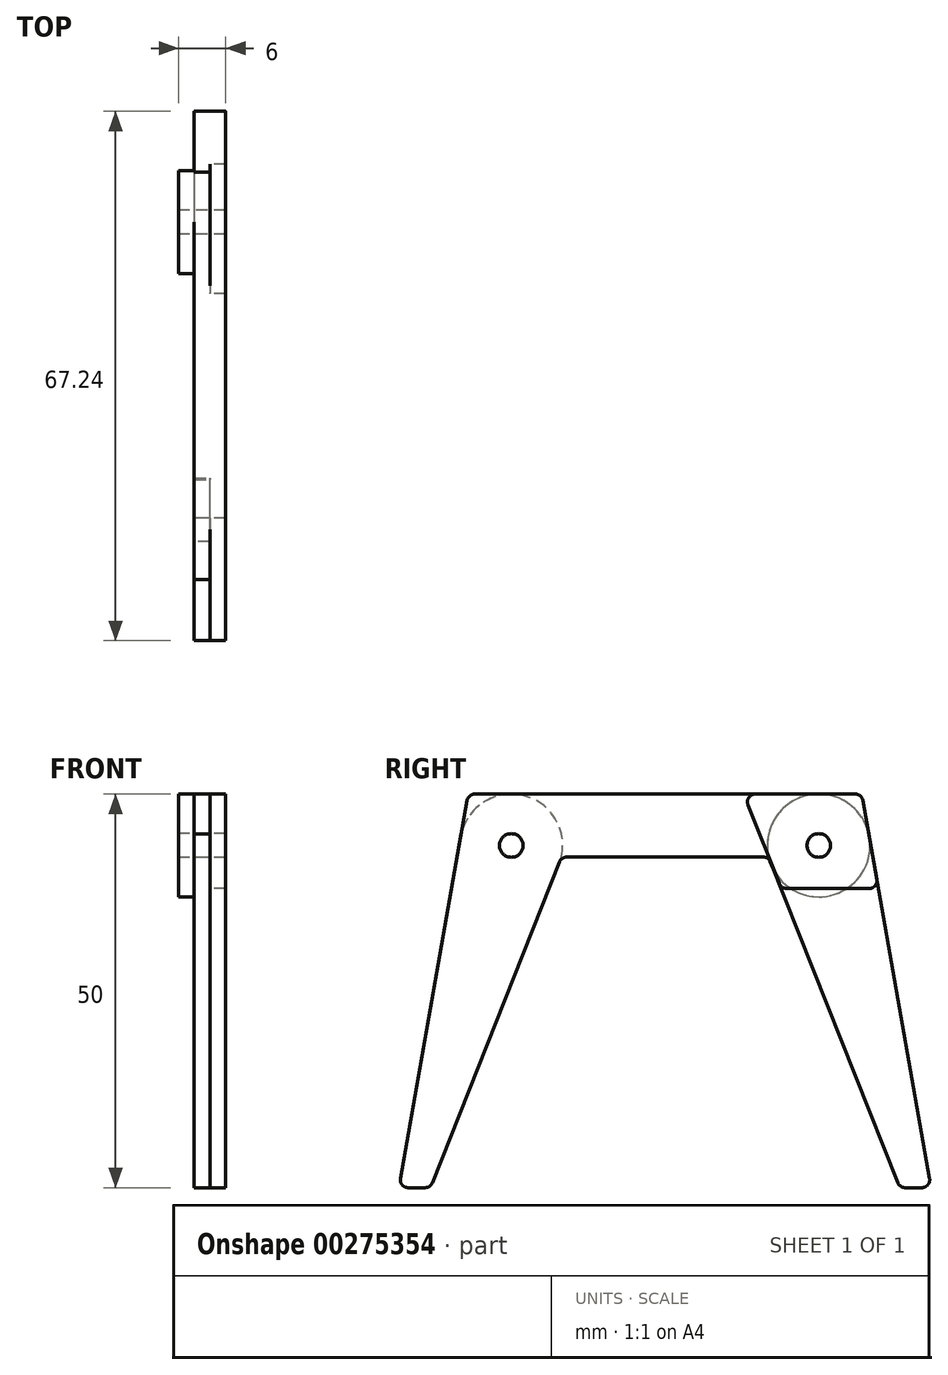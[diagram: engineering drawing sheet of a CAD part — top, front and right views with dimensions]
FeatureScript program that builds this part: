
annotation { "Feature Type Name" : "Feature", "Feature Type Description" : "" }
export const myFeature = defineFeature(function(context is Context, id is Id, definition is map)
    precondition{}
    {
        {
            var Q0;
            Q0=qCreatedBy(makeId("Right.planeOp"),FACE);
            var sketch = newSketch(context, id + "F0", { "sketchPlane" : qUnion([Q0])});
            skLineSegment(sketch, "E0", {"start": v(25.15, 3.17) * mm, "end": v(33.6, -44.83) * mm});
            skLineSegment(sketch, "E1", {"start": v(32.62, -46) * mm, "end": v(30.5, -46) * mm});
            skLineSegment(sketch, "E2", {"start": v(29.57, -45.37) * mm, "end": v(13.42, -4.63) * mm});
            skLineSegment(sketch, "E3", {"start": v(12.5, -4) * mm, "end": v(0, -4) * mm});
            skLineSegment(sketch, "E4", {"start": v(0, -4) * mm, "end": v(0, 4) * mm});
            skLineSegment(sketch, "E5", {"start": v(13.17, -4) * mm, "end": v(10, 4) * mm, "construction": true});
            skLineSegment(sketch, "E6", {"start": v(0, 4) * mm, "end": v(10, 4) * mm});
            skLineSegment(sketch, "E7", {"start": v(24.16, 4) * mm, "end": v(10, 4) * mm});
            skPoint(sketch, "E8.visualSharp", {"position": v(25, 4) * mm});
            skArc(sketch, "E8.filletArc", {"start": v(25.15, 3.17) * mm, "mid": v(24.8, 3.77) * mm, "end": v(24.16, 4) * mm});
            skPoint(sketch, "E9.visualSharp", {"position": v(13.17, -4) * mm});
            skArc(sketch, "E9.filletArc", {"start": v(13.42, -4.63) * mm, "mid": v(13.05, -4.17) * mm, "end": v(12.5, -4) * mm});
            skPoint(sketch, "E10.visualSharp", {"position": v(29.82, -46) * mm});
            skArc(sketch, "E10.filletArc", {"start": v(29.57, -45.37) * mm, "mid": v(29.93, -45.83) * mm, "end": v(30.5, -46) * mm});
            skPoint(sketch, "E11.visualSharp", {"position": v(33.82, -46) * mm});
            skArc(sketch, "E11.filletArc", {"start": v(32.62, -46) * mm, "mid": v(33.4, -45.64) * mm, "end": v(33.6, -44.83) * mm});
            skSolve(sketch);
        }
        {
            var Q0;
            Q0=qCreatedBy(makeId("Right.planeOp"),FACE);
            var sketch = newSketch(context, id + "F1", { "sketchPlane" : qUnion([Q0])});
            skLineSegment(sketch, "E12", {"start": v(25.9, -1.06) * mm, "end": v(33.6, -44.83) * mm});
            skLineSegment(sketch, "E13", {"start": v(32.62, -46) * mm, "end": v(30.5, -46) * mm});
            skLineSegment(sketch, "E14", {"start": v(29.57, -45.37) * mm, "end": v(13.42, -4.63) * mm});
            skLineSegment(sketch, "E15", {"start": v(12.5, -4) * mm, "end": v(0, -4) * mm});
            skLineSegment(sketch, "E16", {"start": v(0, -4) * mm, "end": v(0, 4) * mm});
            skLineSegment(sketch, "E17", {"start": v(13.17, -4) * mm, "end": v(10, 4) * mm, "construction": true});
            skLineSegment(sketch, "E18", {"start": v(0, 4) * mm, "end": v(10, 4) * mm});
            skLineSegment(sketch, "E19", {"start": v(25, 4) * mm, "end": v(19.53, 4) * mm, "construction": true});
            skArc(sketch, "E20", {"start": v(25.9, -1.06) * mm, "mid": v(23.6, 2.58) * mm, "end": v(19.53, 4) * mm});
            skLineSegment(sketch, "E21", {"start": v(13.17, -4) * mm, "end": v(25.9, -1.06) * mm, "construction": true});
            skLineSegment(sketch, "E22", {"start": v(25.9, -1.06) * mm, "end": v(25, 4) * mm, "construction": true});
            skLineSegment(sketch, "E23", {"start": v(19.53, 4) * mm, "end": v(10, 4) * mm});
            skPoint(sketch, "E24.visualSharp", {"position": v(13.17, -4) * mm});
            skArc(sketch, "E24.filletArc", {"start": v(13.42, -4.63) * mm, "mid": v(13.05, -4.17) * mm, "end": v(12.5, -4) * mm});
            skPoint(sketch, "E25.visualSharp", {"position": v(29.82, -46) * mm});
            skArc(sketch, "E25.filletArc", {"start": v(29.57, -45.37) * mm, "mid": v(29.93, -45.83) * mm, "end": v(30.5, -46) * mm});
            skPoint(sketch, "E26.visualSharp", {"position": v(33.82, -46) * mm});
            skArc(sketch, "E26.filletArc", {"start": v(32.62, -46) * mm, "mid": v(33.4, -45.64) * mm, "end": v(33.6, -44.83) * mm});
            skSolve(sketch);
        }
        {
            var Q0;
            Q0=qCreatedBy(makeId("Right.planeOp"),FACE);
            var sketch = newSketch(context, id + "F2", { "sketchPlane" : qUnion([Q0])});
            skLineSegment(sketch, "E27", {"start": v(25.9, -1.06) * mm, "end": v(33.6, -44.83) * mm});
            skLineSegment(sketch, "E28", {"start": v(32.62, -46) * mm, "end": v(30.5, -46) * mm});
            skLineSegment(sketch, "E29", {"start": v(29.57, -45.37) * mm, "end": v(13.17, -4) * mm});
            skLineSegment(sketch, "E30", {"start": v(13.17, -4) * mm, "end": v(0, -4) * mm, "construction": true});
            skLineSegment(sketch, "E31", {"start": v(0, -4) * mm, "end": v(0, 4) * mm, "construction": true});
            skLineSegment(sketch, "E32", {"start": v(13.17, -4) * mm, "end": v(10, 4) * mm, "construction": true});
            skLineSegment(sketch, "E33", {"start": v(0, 4) * mm, "end": v(10, 4) * mm, "construction": true});
            skLineSegment(sketch, "E34", {"start": v(25, 4) * mm, "end": v(19.53, 4) * mm, "construction": true});
            skLineSegment(sketch, "E35", {"start": v(13.17, -4) * mm, "end": v(25.9, -1.06) * mm, "construction": true});
            skLineSegment(sketch, "E36", {"start": v(25.9, -1.06) * mm, "end": v(25, 4) * mm, "construction": true});
            skLineSegment(sketch, "E37", {"start": v(19.53, 4) * mm, "end": v(10, 4) * mm, "construction": true});
            skArc(sketch, "E38", {"start": v(25.9, -1.06) * mm, "mid": v(18.06, 3.83) * mm, "end": v(13.17, -4) * mm});
            skPoint(sketch, "E39.visualSharp", {"position": v(29.82, -46) * mm});
            skArc(sketch, "E39.filletArc", {"start": v(29.57, -45.37) * mm, "mid": v(29.93, -45.83) * mm, "end": v(30.5, -46) * mm});
            skPoint(sketch, "E40.visualSharp", {"position": v(33.82, -46) * mm});
            skArc(sketch, "E40.filletArc", {"start": v(32.62, -46) * mm, "mid": v(33.4, -45.64) * mm, "end": v(33.6, -44.83) * mm});
            skSolve(sketch);
        }
        {
            var Q0;
            Q0=qCreatedBy(makeId("Right.planeOp"),FACE);
            var sketch = newSketch(context, id + "F3", { "sketchPlane" : qUnion([Q0])});
            skLineSegment(sketch, "E41", {"start": v(25.9, -1.06) * mm, "end": v(33.6, -44.83) * mm, "construction": true});
            skLineSegment(sketch, "E42", {"start": v(32.62, -46) * mm, "end": v(30.5, -46) * mm, "construction": true});
            skLineSegment(sketch, "E43", {"start": v(29.57, -45.37) * mm, "end": v(13.17, -4) * mm, "construction": true});
            skLineSegment(sketch, "E44", {"start": v(13.17, -4) * mm, "end": v(0, -4) * mm, "construction": true});
            skLineSegment(sketch, "E45", {"start": v(0, -4) * mm, "end": v(0, 4) * mm, "construction": true});
            skLineSegment(sketch, "E46", {"start": v(13.17, -4) * mm, "end": v(10, 4) * mm, "construction": true});
            skLineSegment(sketch, "E47", {"start": v(0, 4) * mm, "end": v(10, 4) * mm, "construction": true});
            skLineSegment(sketch, "E48", {"start": v(25, 4) * mm, "end": v(19.53, 4) * mm, "construction": true});
            skLineSegment(sketch, "E49", {"start": v(13.17, -4) * mm, "end": v(25.9, -1.06) * mm, "construction": true});
            skLineSegment(sketch, "E50", {"start": v(25.9, -1.06) * mm, "end": v(25, 4) * mm, "construction": true});
            skLineSegment(sketch, "E51", {"start": v(19.53, 4) * mm, "end": v(10, 4) * mm, "construction": true});
            skArc(sketch, "E52", {"start": v(25.9, -1.06) * mm, "mid": v(18.06, 3.83) * mm, "end": v(13.17, -4) * mm, "construction": true});
            skPoint(sketch, "E53.visualSharp", {"position": v(29.82, -46) * mm});
            skArc(sketch, "E53.filletArc", {"start": v(29.57, -45.37) * mm, "mid": v(29.93, -45.83) * mm, "end": v(30.5, -46) * mm, "construction": true});
            skPoint(sketch, "E54.visualSharp", {"position": v(33.82, -46) * mm});
            skArc(sketch, "E54.filletArc", {"start": v(32.62, -46) * mm, "mid": v(33.4, -45.64) * mm, "end": v(33.6, -44.83) * mm, "construction": true});
            skCircle(sketch, "E55", {"center": v(19.53, -2.53) * mm, "radius": 1.5 * mm});
            skCircle(sketch, "E56.MirrorC", {"center": v(-19.53, -2.53) * mm, "radius": 1.5 * mm});
            skSolve(sketch);
        }
        {
            var Q0;
            Q0=qCreatedBy(makeId("Right.planeOp"),FACE);
            var sketch = newSketch(context, id + "F4", { "sketchPlane" : qUnion([Q0])});
            skLineSegment(sketch, "E57", {"start": v(25.9, -1.06) * mm, "end": v(26.9, -6.83) * mm});
            skLineSegment(sketch, "E58", {"start": v(32.62, -46) * mm, "end": v(30.5, -46) * mm, "construction": true});
            skLineSegment(sketch, "E59", {"start": v(29.57, -45.37) * mm, "end": v(14.76, -8) * mm, "construction": true});
            skLineSegment(sketch, "E60", {"start": v(13.17, -4) * mm, "end": v(0, -4) * mm, "construction": true});
            skLineSegment(sketch, "E61", {"start": v(0, -4) * mm, "end": v(0, 4) * mm, "construction": true});
            skLineSegment(sketch, "E62", {"start": v(13.17, -4) * mm, "end": v(10.54, 2.63) * mm});
            skLineSegment(sketch, "E63", {"start": v(0, 4) * mm, "end": v(10, 4) * mm, "construction": true});
            skLineSegment(sketch, "E64", {"start": v(24.16, 4) * mm, "end": v(19.53, 4) * mm});
            skLineSegment(sketch, "E65", {"start": v(13.17, -4) * mm, "end": v(25.9, -1.06) * mm, "construction": true});
            skLineSegment(sketch, "E66", {"start": v(25.9, -1.06) * mm, "end": v(25.15, 3.17) * mm});
            skLineSegment(sketch, "E67", {"start": v(19.53, 4) * mm, "end": v(11.47, 4) * mm});
            skArc(sketch, "E68", {"start": v(25.9, -1.06) * mm, "mid": v(18.06, 3.83) * mm, "end": v(13.17, -4) * mm, "construction": true});
            skPoint(sketch, "E69.visualSharp", {"position": v(29.82, -46) * mm});
            skArc(sketch, "E69.filletArc", {"start": v(29.57, -45.37) * mm, "mid": v(29.93, -45.83) * mm, "end": v(30.5, -46) * mm, "construction": true});
            skPoint(sketch, "E70.visualSharp", {"position": v(33.82, -46) * mm});
            skArc(sketch, "E70.filletArc", {"start": v(32.62, -46) * mm, "mid": v(33.4, -45.64) * mm, "end": v(33.6, -44.83) * mm, "construction": true});
            skCircle(sketch, "E71", {"center": v(19.53, -2.53) * mm, "radius": 1.5 * mm});
            skLineSegment(sketch, "E72", {"start": v(15.44, -8) * mm, "end": v(25.92, -8) * mm});
            skLineSegment(sketch, "E73", {"start": v(14.5, -7.37) * mm, "end": v(13.17, -4) * mm});
            skLineSegment(sketch, "E74", {"start": v(27.12, -8) * mm, "end": v(33.6, -44.83) * mm, "construction": true});
            skPoint(sketch, "E75.visualSharp", {"position": v(25, 4) * mm});
            skArc(sketch, "E75.filletArc", {"start": v(25.15, 3.17) * mm, "mid": v(24.8, 3.77) * mm, "end": v(24.16, 4) * mm});
            skPoint(sketch, "E76.visualSharp", {"position": v(27.12, -8) * mm});
            skArc(sketch, "E76.filletArc", {"start": v(25.92, -8) * mm, "mid": v(26.7, -7.64) * mm, "end": v(26.9, -6.83) * mm});
            skPoint(sketch, "E77.visualSharp", {"position": v(14.76, -8) * mm});
            skArc(sketch, "E77.filletArc", {"start": v(14.5, -7.37) * mm, "mid": v(14.87, -7.83) * mm, "end": v(15.44, -8) * mm});
            skPoint(sketch, "E78.visualSharp", {"position": v(10, 4) * mm});
            skArc(sketch, "E78.filletArc", {"start": v(11.47, 4) * mm, "mid": v(10.64, 3.56) * mm, "end": v(10.54, 2.63) * mm});
            skSolve(sketch);
        }
        {
            var Q0;
            Q0=makeQuery(id+"F0.imprint","IMPRINT",FACE,{"disambiguationData":[TD([[makeQuery(id+"F0.imprint","IMPRINT",EDGE,{"derivedFrom":sQuery(id+"F0.wireOp",EDGE,"E0")}),-1.0]])]});
            extrude(context, id + "F5", {"entities" : qUnion([Q0]), "depth" : 2 * mm, "offsetDistance" : 25 * mm});
        }
        {
            var Q0;
            Q0=makeQuery(id+"F5.opExtrude","SWEPT_BODY",BODY,{"disambiguationData":[OSD([sQuery(id+"F0.wireOp",EDGE,"E0"),sQuery(id+"F0.wireOp",EDGE,"E1"),sQuery(id+"F0.wireOp",EDGE,"E2"),sQuery(id+"F0.wireOp",EDGE,"E3"),sQuery(id+"F0.wireOp",EDGE,"E4"),sQuery(id+"F0.wireOp",EDGE,"E6"),sQuery(id+"F0.wireOp",EDGE,"E7")])]});
            var Q1;
            Q1=qCreatedBy(makeId("Front.planeOp"),FACE);
            mirror(context, id + "F6", {"operationType" : NewBodyOperationType.ADD, "entities" : qUnion([Q0]), "mirrorPlane" : qUnion([Q1])});
        }
        {
            var Q0;
            Q0=makeQuery(id+"F1.imprint","IMPRINT",FACE,{"disambiguationData":[TD([[makeQuery(id+"F1.imprint","IMPRINT",EDGE,{"derivedFrom":sQuery(id+"F1.wireOp",EDGE,"E12")}),-1.0]])]});
            extrude(context, id + "F7", {"entities" : qUnion([Q0]), "oppositeDirection" : true, "depth" : 2 * mm, "offsetDistance" : 25 * mm});
        }
        {
            var Q0;
            Q0=makeQuery(id+"F7.opExtrude","SWEPT_BODY",BODY,{"disambiguationData":[OSD([sQuery(id+"F1.wireOp",EDGE,"E12"),sQuery(id+"F1.wireOp",EDGE,"E13"),sQuery(id+"F1.wireOp",EDGE,"E14"),sQuery(id+"F1.wireOp",EDGE,"E15"),sQuery(id+"F1.wireOp",EDGE,"E16"),sQuery(id+"F1.wireOp",EDGE,"E18"),sQuery(id+"F1.wireOp",EDGE,"E20"),sQuery(id+"F1.wireOp",EDGE,"E23")])]});
            var Q1;
            Q1=qCreatedBy(makeId("Front.planeOp"),FACE);
            mirror(context, id + "F8", {"operationType" : NewBodyOperationType.ADD, "entities" : qUnion([Q0]), "mirrorPlane" : qUnion([Q1])});
        }
        {
            var Q0;
            Q0 = qSketchRegion(id + "F2", true);
            extrude(context, id + "F9", {"entities" : qUnion([Q0]), "oppositeDirection" : true, "depth" : 2 * mm, "offsetDistance" : 25 * mm});
        }
        {
            var Q0;
            Q0=makeQuery(id+"F9.opExtrude","SWEPT_BODY",BODY,{"disambiguationData":[OSD([sQuery(id+"F2.wireOp",EDGE,"E27"),sQuery(id+"F2.wireOp",EDGE,"E28"),sQuery(id+"F2.wireOp",EDGE,"E29"),sQuery(id+"F2.wireOp",EDGE,"E38")])]});
            var Q1;
            Q1=qCreatedBy(makeId("Front.planeOp"),FACE);
            mirror(context, id + "F10", {"entities" : qUnion([Q0]), "mirrorPlane" : qUnion([Q1])});
        }
        {
            var Q0;
            Q0 = qSketchRegion(id + "F3", true);
            var Q1;
            Q1=sQuery(id+"F3.wireOp",EDGE,"E55");
            extrude(context, id + "F11", {"entities" : qUnion([Q0]), "operationType" : NewBodyOperationType.REMOVE, "surfaceEntities" : qUnion([Q1]), "depth" : 25 * mm, "offsetDistance" : 25 * mm, "symmetric" : true});
        }
        {
            var Q0;
            Q0=makeQuery(id+"F9.opExtrude","CAP_FACE",FACE,{"disambiguationData":[OSD([sQuery(id+"F2.wireOp",EDGE,"E27"),sQuery(id+"F2.wireOp",EDGE,"E28"),sQuery(id+"F2.wireOp",EDGE,"E29"),sQuery(id+"F2.wireOp",EDGE,"E38"),sQuery(id+"F2.wireOp",EDGE,"E39.filletArc"),sQuery(id+"F2.wireOp",EDGE,"E40.filletArc")])],"isStart":false});
            var sketch = newSketch(context, id + "F12", { "sketchPlane" : qUnion([Q0])});
            skCircle(sketch, "E79", {"center": v(-19.53, -2.53) * mm, "radius": 1.5 * mm});
            skCircle(sketch, "E80", {"center": v(-19.53, -2.53) * mm, "radius": 6.53 * mm});
            skSolve(sketch);
        }
        {
            var Q0;
            Q0 = qSketchRegion(id + "F12", true);
            extrude(context, id + "F13", {"entities" : qUnion([Q0]), "operationType" : NewBodyOperationType.ADD, "depth" : 2 * mm, "offsetDistance" : 25 * mm});
        }
        {
            var Q0;
            Q0 = qSketchRegion(id + "F4", true);
            extrude(context, id + "F14", {"entities" : qUnion([Q0]), "depth" : 2 * mm, "offsetDistance" : 25 * mm});
        }
    });
